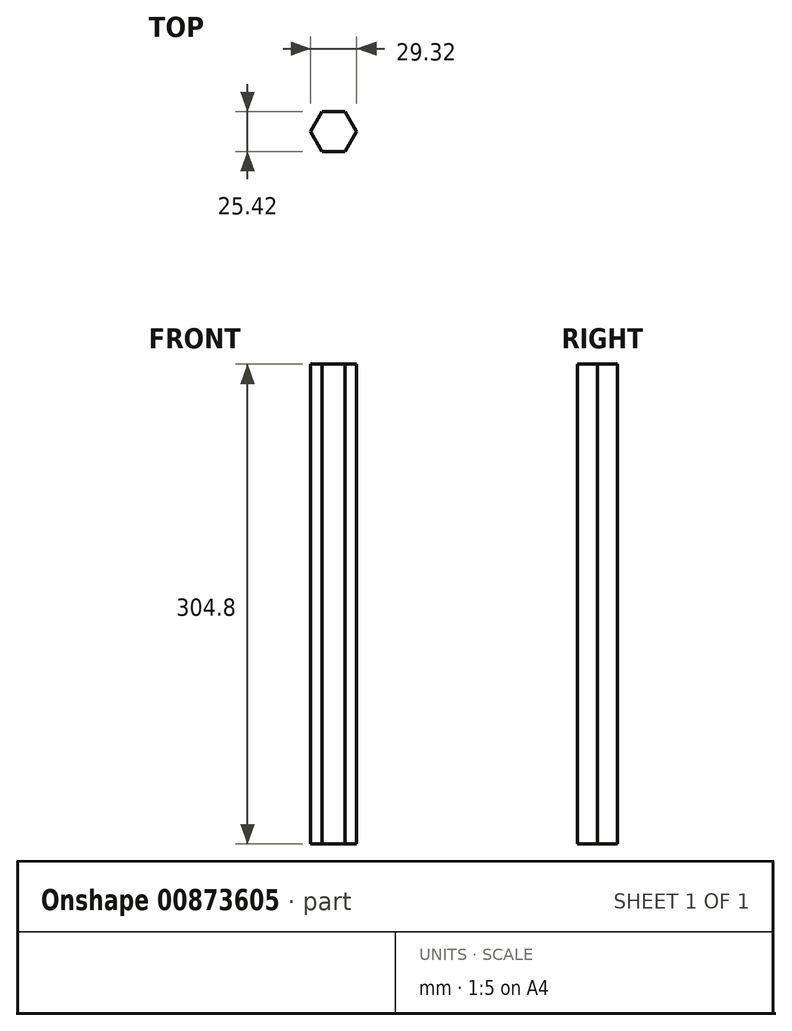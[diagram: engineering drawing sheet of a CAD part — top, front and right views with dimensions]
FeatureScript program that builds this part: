
annotation { "Feature Type Name" : "Feature", "Feature Type Description" : "" }
export const myFeature = defineFeature(function(context is Context, id is Id, definition is map)
    precondition{}
    {
        {
            var Q0;
            Q0=qCreatedBy(makeId("Top.planeOp"),FACE);
            var sketch = newSketch(context, id + "F0", { "sketchPlane" : qUnion([Q0])});
            skCircle(sketch, "E0.cCircle", {"center": v(0, 0) * mm, "radius": 12.7 * mm, "construction": true});
            skLineSegment(sketch, "E0.0", {"start": v(7.32, 12.7) * mm, "end": v(14.66, 0.02) * mm});
            skLineSegment(sketch, "E0.1", {"start": v(14.66, 0.02) * mm, "end": v(7.35, -12.7) * mm});
            skLineSegment(sketch, "E0.2", {"start": v(7.35, -12.7) * mm, "end": v(-7.32, -12.7) * mm});
            skLineSegment(sketch, "E0.3", {"start": v(-7.32, -12.7) * mm, "end": v(-14.66, -0.02) * mm});
            skLineSegment(sketch, "E0.4", {"start": v(-14.66, -0.02) * mm, "end": v(-7.35, 12.7) * mm});
            skLineSegment(sketch, "E0.5", {"start": v(-7.35, 12.7) * mm, "end": v(7.32, 12.7) * mm});
            skPoint(sketch, "E0.0.midPoint", {"position": v(11, 6.36) * mm});
            skSolve(sketch);
        }
        {
            var Q0;
            Q0=makeQuery(id+"F0.imprint","IMPRINT",FACE,{"disambiguationData":[TD([[makeQuery(id+"F0.imprint","IMPRINT",EDGE,{"derivedFrom":sQuery(id+"F0.wireOp",EDGE,"E0.0")}),-1.0]])]});
            extrude(context, id + "F1", {"entities" : qUnion([Q0]), "depth" : 304.8 * mm, "offsetDistance" : 25.4 * mm});
        }
    });
